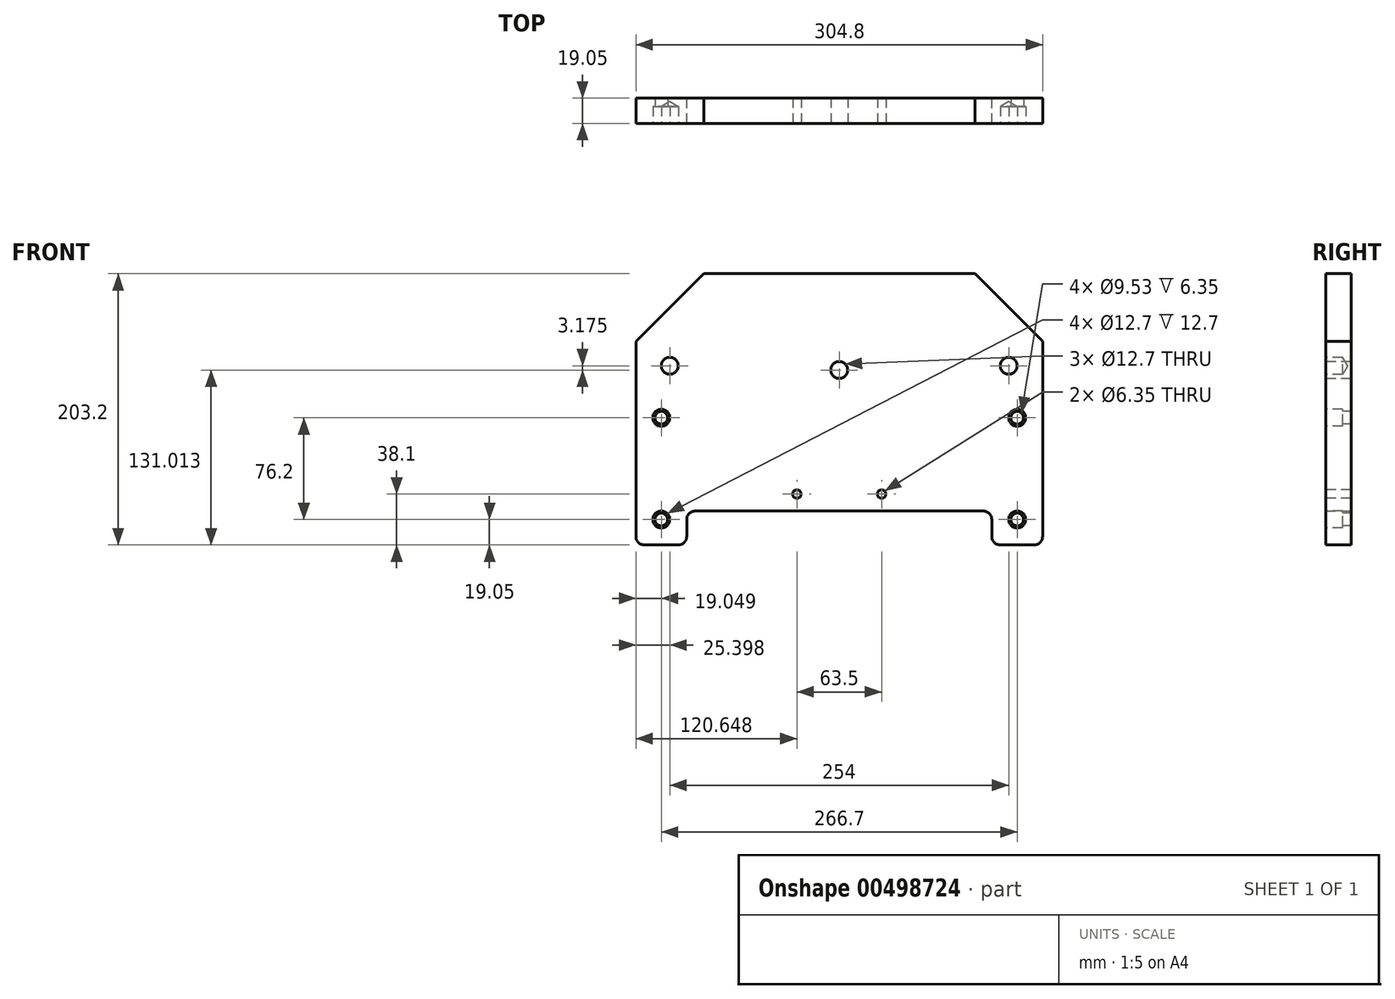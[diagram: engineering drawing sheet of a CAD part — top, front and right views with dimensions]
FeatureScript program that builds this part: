
annotation { "Feature Type Name" : "Feature", "Feature Type Description" : "" }
export const myFeature = defineFeature(function(context is Context, id is Id, definition is map)
    precondition{}
    {
        {
            var Q0;
            Q0=qCreatedBy(makeId("Front.planeOp"),FACE);
            var sketch = newSketch(context, id + "F0", { "sketchPlane" : qUnion([Q0])});
            skLineSegment(sketch, "E0", {"start": v(-61.53, -19.05) * mm, "end": v(-23.43, -19.05) * mm});
            skLineSegment(sketch, "E1", {"start": v(-23.43, -19.05) * mm, "end": v(-23.43, 6.35) * mm});
            skLineSegment(sketch, "E2", {"start": v(-23.43, 6.35) * mm, "end": v(205.17, 6.35) * mm});
            skLineSegment(sketch, "E3", {"start": v(205.17, 6.35) * mm, "end": v(205.17, -19.05) * mm});
            skLineSegment(sketch, "E4", {"start": v(205.17, -19.05) * mm, "end": v(243.27, -19.05) * mm});
            skLineSegment(sketch, "E5", {"start": v(243.27, -19.05) * mm, "end": v(243.27, 184.15) * mm});
            skLineSegment(sketch, "E6", {"start": v(243.27, 184.15) * mm, "end": v(-61.53, 184.15) * mm});
            skLineSegment(sketch, "E7", {"start": v(-61.53, 184.15) * mm, "end": v(-61.53, -19.05) * mm});
            skSolve(sketch);
        }
        {
            var Q0;
            Q0=qSketchRegion(id+"F0",true);
            extrude(context, id + "F1", {"entities" : qUnion([Q0]), "depth" : 19.05 * mm});
        }
        {
            var Q0;
            Q0=makeQuery(id+"F1.opExtrude","SWEPT_EDGE",EDGE,{"disambiguationData":[OSD([sQuery(id+"F0.wireOp",EDGE,"E1"),sQuery(id+"F0.wireOp",EDGE,"E2")])]});
            var Q1;
            Q1=makeQuery(id+"F1.opExtrude","SWEPT_EDGE",EDGE,{"disambiguationData":[OSD([sQuery(id+"F0.wireOp",EDGE,"E0"),sQuery(id+"F0.wireOp",EDGE,"E7")])]});
            var Q2;
            Q2=makeQuery(id+"F1.opExtrude","SWEPT_EDGE",EDGE,{"disambiguationData":[OSD([sQuery(id+"F0.wireOp",EDGE,"E4"),sQuery(id+"F0.wireOp",EDGE,"E5")])]});
            var Q3;
            Q3=makeQuery(id+"F1.opExtrude","SWEPT_EDGE",EDGE,{"disambiguationData":[OSD([sQuery(id+"F0.wireOp",EDGE,"E3"),sQuery(id+"F0.wireOp",EDGE,"E4")])]});
            var Q4;
            Q4=makeQuery(id+"F1.opExtrude","SWEPT_EDGE",EDGE,{"disambiguationData":[OSD([sQuery(id+"F0.wireOp",EDGE,"E2"),sQuery(id+"F0.wireOp",EDGE,"E3")])]});
            var Q5;
            Q5=makeQuery(id+"F1.opExtrude","SWEPT_EDGE",EDGE,{"disambiguationData":[OSD([sQuery(id+"F0.wireOp",EDGE,"E0"),sQuery(id+"F0.wireOp",EDGE,"E1")])]});
            fillet(context, id + "F2", {"entities" : qUnion([Q0, Q1, Q2, Q3, Q4, Q5]), "radius" : 6.35 * mm, "tangentPropagation" : true, "allowEdgeOverflow" : false});
        }
        {
            var Q0;
            Q0=makeQuery(id+"F1.opExtrude","SWEPT_EDGE",EDGE,{"disambiguationData":[OSD([sQuery(id+"F0.wireOp",EDGE,"E5"),sQuery(id+"F0.wireOp",EDGE,"E6")])]});
            var Q1;
            Q1=makeQuery(id+"F1.opExtrude","SWEPT_EDGE",EDGE,{"disambiguationData":[OSD([sQuery(id+"F0.wireOp",EDGE,"E6"),sQuery(id+"F0.wireOp",EDGE,"E7")])]});
            chamfer(context, id + "F3", {"entities" : qUnion([Q0, Q1]), "chamferType" : ChamferType.OFFSET_ANGLE, "width" : 50.8 * mm, "oppositeDirection" : false, "angle" : 45 * degree, "tangentPropagation" : true});
        }
        {
            var Q0;
            Q0=makeQuery(id+"F1.opExtrude","CAP_FACE",FACE,{"disambiguationData":[OSD([sQuery(id+"F0.wireOp",EDGE,"E0"),sQuery(id+"F0.wireOp",EDGE,"E1"),sQuery(id+"F0.wireOp",EDGE,"E2"),sQuery(id+"F0.wireOp",EDGE,"E3"),sQuery(id+"F0.wireOp",EDGE,"E4"),sQuery(id+"F0.wireOp",EDGE,"E5"),sQuery(id+"F0.wireOp",EDGE,"E6"),sQuery(id+"F0.wireOp",EDGE,"E7")])],"isStart":false});
            var sketch = newSketch(context, id + "F4", { "sketchPlane" : qUnion([Q0])});
            skCircle(sketch, "E8", {"center": v(90.87, 111.96) * mm, "radius": 6.35 * mm});
            skCircle(sketch, "E9", {"center": v(217.87, 115.14) * mm, "radius": 6.35 * mm});
            skCircle(sketch, "E10", {"center": v(-36.13, 115.14) * mm, "radius": 6.35 * mm});
            skCircle(sketch, "E11", {"center": v(59.12, 19.05) * mm, "radius": 3.18 * mm});
            skCircle(sketch, "E12", {"center": v(122.62, 19.05) * mm, "radius": 3.17 * mm});
            skCircle(sketch, "E13", {"center": v(-42.48, 0) * mm, "radius": 6.35 * mm});
            skCircle(sketch, "E14", {"center": v(-42.48, 76.2) * mm, "radius": 6.35 * mm});
            skCircle(sketch, "E15", {"center": v(224.22, 76.2) * mm, "radius": 6.35 * mm});
            skCircle(sketch, "E16", {"center": v(224.22, 0) * mm, "radius": 6.35 * mm});
            skSolve(sketch);
        }
        {
            var Q0;
            Q0=makeQuery(id+"F4.imprint","IMPRINT",FACE,{"disambiguationData":[TD([[makeQuery(id+"F4.imprint","IMPRINT",EDGE,{"derivedFrom":sQuery(id+"F4.wireOp",EDGE,"E8")}),1.0]])]});
            var Q1;
            Q1=makeQuery(id+"F4.imprint","IMPRINT",FACE,{"disambiguationData":[TD([[makeQuery(id+"F4.imprint","IMPRINT",EDGE,{"derivedFrom":sQuery(id+"F4.wireOp",EDGE,"E11")}),1.0]])]});
            var Q2;
            Q2=makeQuery(id+"F4.imprint","IMPRINT",FACE,{"disambiguationData":[TD([[makeQuery(id+"F4.imprint","IMPRINT",EDGE,{"derivedFrom":sQuery(id+"F4.wireOp",EDGE,"E12")}),1.0]])]});
            extrude(context, id + "F5", {"entities" : qUnion([Q0, Q1, Q2]), "operationType" : NewBodyOperationType.REMOVE, "oppositeDirection" : true, "depth" : 25.4 * mm});
        }
        {
            var Q0;
            Q0=sQuery(id+"F4.wireOp",VERTEX,"E10.center");
            var Q1;
            Q1=sQuery(id+"F4.wireOp",VERTEX,"E9.center");
            var Q2;
            Q2=makeQuery(id+"F1.opExtrude","SWEPT_BODY",BODY,{"disambiguationData":[OSD([sQuery(id+"F0.wireOp",EDGE,"E0"),sQuery(id+"F0.wireOp",EDGE,"E1"),sQuery(id+"F0.wireOp",EDGE,"E2"),sQuery(id+"F0.wireOp",EDGE,"E3"),sQuery(id+"F0.wireOp",EDGE,"E4"),sQuery(id+"F0.wireOp",EDGE,"E5"),sQuery(id+"F0.wireOp",EDGE,"E6"),sQuery(id+"F0.wireOp",EDGE,"E7")])]});
            hole(context, id + "F6", {"style" : HoleStyle.SIMPLE, "endStyle" : HoleEndStyle.BLIND, "holeDiameter" : 12.7 * mm, "holeDepth" : 12.7 * mm, "tappedDepth" : 12.7 * mm, "tapClearance" : 3, "startFromSketch" : true, "locations" : qUnion([Q0, Q1]), "scope" : qUnion([Q2])});
        }
        {
            var Q0;
            Q0=sQuery(id+"F4.wireOp",VERTEX,"E14.center");
            var Q1;
            Q1=sQuery(id+"F4.wireOp",VERTEX,"E13.center");
            var Q2;
            Q2=sQuery(id+"F4.wireOp",VERTEX,"E16.center");
            var Q3;
            Q3=sQuery(id+"F4.wireOp",VERTEX,"E15.center");
            var Q4;
            Q4=makeQuery(id+"F1.opExtrude","SWEPT_BODY",BODY,{"disambiguationData":[OSD([sQuery(id+"F0.wireOp",EDGE,"E0"),sQuery(id+"F0.wireOp",EDGE,"E1"),sQuery(id+"F0.wireOp",EDGE,"E2"),sQuery(id+"F0.wireOp",EDGE,"E3"),sQuery(id+"F0.wireOp",EDGE,"E4"),sQuery(id+"F0.wireOp",EDGE,"E5"),sQuery(id+"F0.wireOp",EDGE,"E6"),sQuery(id+"F0.wireOp",EDGE,"E7")])]});
            hole(context, id + "F7", {"style" : HoleStyle.C_BORE, "endStyle" : HoleEndStyle.BLIND, "holeDiameter" : 9.52 * mm, "cBoreDiameter" : 12.7 * mm, "cBoreDepth" : 12.7 * mm, "holeDepth" : 25.4 * mm, "tappedDepth" : 12.7 * mm, "tapClearance" : 3, "startFromSketch" : true, "locations" : qUnion([Q0, Q1, Q2, Q3]), "scope" : qUnion([Q4])});
        }
    });
